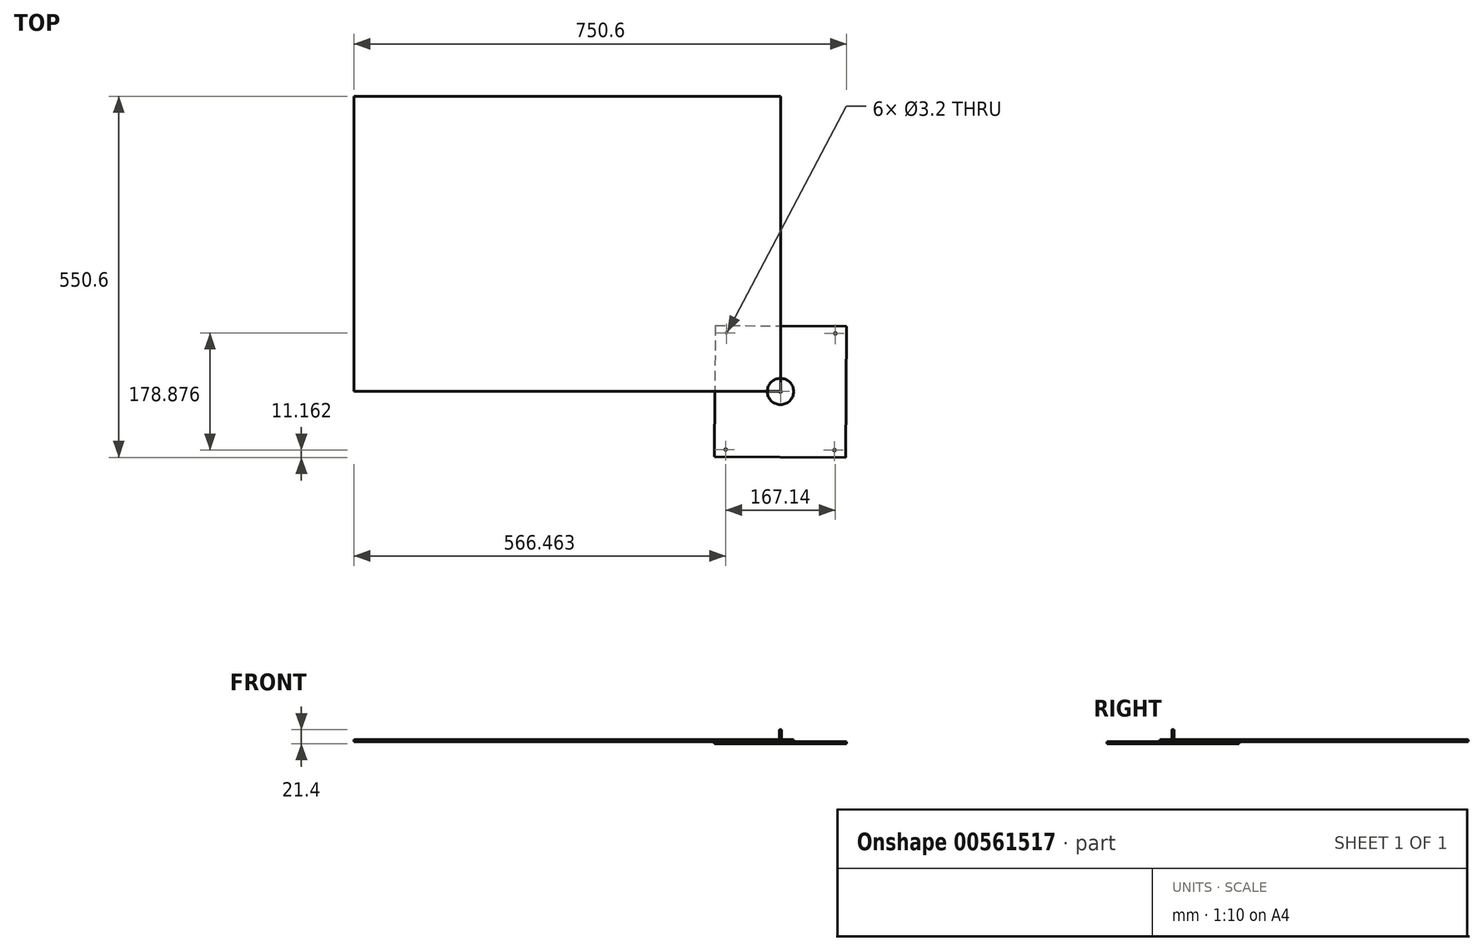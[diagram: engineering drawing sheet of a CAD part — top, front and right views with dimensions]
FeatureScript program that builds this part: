
annotation { "Feature Type Name" : "Feature", "Feature Type Description" : "" }
export const myFeature = defineFeature(function(context is Context, id is Id, definition is map)
    precondition{}
    {
        {
            var Q0;
            Q0=qCreatedBy(makeId("Top.planeOp"),FACE);
            var sketch = newSketch(context, id + "F0", { "sketchPlane" : qUnion([Q0])});
            skLineSegment(sketch, "E0.bottom", {"start": v(-99.4, 100.6) * mm, "end": v(100.6, 99.4) * mm});
            skLineSegment(sketch, "E0.top", {"start": v(-100.6, -99.4) * mm, "end": v(99.4, -100.6) * mm});
            skLineSegment(sketch, "E0.left", {"start": v(-99.4, 100.6) * mm, "end": v(-100.6, -99.4) * mm});
            skLineSegment(sketch, "E0.right", {"start": v(100.6, 99.4) * mm, "end": v(99.4, -100.6) * mm});
            skCircle(sketch, "E1", {"center": v(-83.54, -88.43) * mm, "radius": 1.6 * mm});
            skCircle(sketch, "E2", {"center": v(-82.4, 89.44) * mm, "radius": 1.6 * mm});
            skCircle(sketch, "E3", {"center": v(83.6, 88.43) * mm, "radius": 1.6 * mm});
            skCircle(sketch, "E4", {"center": v(82.4, -89.44) * mm, "radius": 1.6 * mm});
            skCircle(sketch, "E5", {"center": v(0, 0) * mm, "radius": 1.6 * mm});
            skSolve(sketch);
        }
        {
            var Q0;
            Q0=makeQuery(id+"F0.imprint","IMPRINT",FACE,{"disambiguationData":[TD([[makeQuery(id+"F0.imprint","IMPRINT",EDGE,{"derivedFrom":sQuery(id+"F0.wireOp",EDGE,"E0.bottom")}),-1.0]])]});
            extrude(context, id + "F1", {"entities" : qUnion([Q0]), "depth" : 3.2 * mm});
        }
        {
            var Q0;
            Q0=makeQuery(id+"F1.opExtrude","CAP_FACE",FACE,{"disambiguationData":[OSD([sQuery(id+"F0.wireOp",EDGE,"E0.bottom"),sQuery(id+"F0.wireOp",EDGE,"E0.top"),sQuery(id+"F0.wireOp",EDGE,"E0.left"),sQuery(id+"F0.wireOp",EDGE,"E0.right"),sQuery(id+"F0.wireOp",EDGE,"89cafc2f-88e5-4794-8ebe-84d65b012602.0"),sQuery(id+"F0.wireOp",EDGE,"89cafc2f-88e5-4794-8ebe-84d65b012602.1"),sQuery(id+"F0.wireOp",EDGE,"89cafc2f-88e5-4794-8ebe-84d65b012602.2"),sQuery(id+"F0.wireOp",EDGE,"89cafc2f-88e5-4794-8ebe-84d65b012602.3"),sQuery(id+"F0.wireOp",EDGE,"89cafc2f-88e5-4794-8ebe-84d65b012602.4"),sQuery(id+"F0.wireOp",EDGE,"89cafc2f-88e5-4794-8ebe-84d65b012602.5"),sQuery(id+"F0.wireOp",EDGE,"56885d26-f8c7-44ec-aa15-5e09e0dd8a5c.0"),sQuery(id+"F0.wireOp",EDGE,"56885d26-f8c7-44ec-aa15-5e09e0dd8a5c.1"),sQuery(id+"F0.wireOp",EDGE,"56885d26-f8c7-44ec-aa15-5e09e0dd8a5c.2"),sQuery(id+"F0.wireOp",EDGE,"56885d26-f8c7-44ec-aa15-5e09e0dd8a5c.3"),sQuery(id+"F0.wireOp",EDGE,"56885d26-f8c7-44ec-aa15-5e09e0dd8a5c.4"),sQuery(id+"F0.wireOp",EDGE,"56885d26-f8c7-44ec-aa15-5e09e0dd8a5c.5"),sQuery(id+"F0.wireOp",EDGE,"f2c23d00-8595-49d7-9619-0574d8eb3167.0"),sQuery(id+"F0.wireOp",EDGE,"f2c23d00-8595-49d7-9619-0574d8eb3167.1"),sQuery(id+"F0.wireOp",EDGE,"f2c23d00-8595-49d7-9619-0574d8eb3167.2"),sQuery(id+"F0.wireOp",EDGE,"f2c23d00-8595-49d7-9619-0574d8eb3167.3"),sQuery(id+"F0.wireOp",EDGE,"f2c23d00-8595-49d7-9619-0574d8eb3167.4"),sQuery(id+"F0.wireOp",EDGE,"f2c23d00-8595-49d7-9619-0574d8eb3167.5"),sQuery(id+"F0.wireOp",EDGE,"5ac249ba-4f04-493e-8005-cd37f262696a.0"),sQuery(id+"F0.wireOp",EDGE,"5ac249ba-4f04-493e-8005-cd37f262696a.1"),sQuery(id+"F0.wireOp",EDGE,"5ac249ba-4f04-493e-8005-cd37f262696a.2"),sQuery(id+"F0.wireOp",EDGE,"5ac249ba-4f04-493e-8005-cd37f262696a.3"),sQuery(id+"F0.wireOp",EDGE,"5ac249ba-4f04-493e-8005-cd37f262696a.4"),sQuery(id+"F0.wireOp",EDGE,"5ac249ba-4f04-493e-8005-cd37f262696a.5")])],"isStart":false});
            var sketch = newSketch(context, id + "F2", { "sketchPlane" : qUnion([Q0])});
            skCircle(sketch, "E6", {"center": v(0, 0) * mm, "radius": 20 * mm});
            skCircle(sketch, "E7", {"center": v(0, 0) * mm, "radius": 0.95 * mm});
            skSolve(sketch);
        }
        {
            var Q0;
            Q0=makeQuery(id+"F2.imprint","IMPRINT",FACE,{"disambiguationData":[TD([[makeQuery(id+"F2.imprint","IMPRINT",EDGE,{"derivedFrom":sQuery(id+"F2.wireOp",EDGE,"E6")}),1.0]])]});
            extrude(context, id + "F3", {"entities" : qUnion([Q0]), "depth" : 3.2 * mm});
        }
        {
            var Q0;
            Q0=makeQuery(id+"F3.opExtrude","CAP_FACE",FACE,{"disambiguationData":[OSD([sQuery(id+"F2.wireOp",EDGE,"E6"),sQuery(id+"F2.wireOp",EDGE,"E7")])],"isStart":false});
            var sketch = newSketch(context, id + "F4", { "sketchPlane" : qUnion([Q0])});
            skCircle(sketch, "E8", {"center": v(0, 0) * mm, "radius": 1.6 * mm});
            skSolve(sketch);
        }
        {
            var Q0;
            Q0=makeQuery(id+"F4.imprint","IMPRINT",FACE,{"disambiguationData":[TD([[makeQuery(id+"F4.imprint","IMPRINT",EDGE,{"derivedFrom":sQuery(id+"F4.wireOp",EDGE,"E8")}),1.0]])]});
            extrude(context, id + "F5", {"entities" : qUnion([Q0]), "depth" : 15 * mm, "offsetDistance" : 25 * mm});
        }
        {
            var Q0;
            Q0=makeQuery(id+"F1.opExtrude","CAP_FACE",FACE,{"disambiguationData":[OSD([sQuery(id+"F0.wireOp",EDGE,"E0.bottom"),sQuery(id+"F0.wireOp",EDGE,"E0.top"),sQuery(id+"F0.wireOp",EDGE,"E0.left"),sQuery(id+"F0.wireOp",EDGE,"E0.right"),sQuery(id+"F0.wireOp",EDGE,"E1"),sQuery(id+"F0.wireOp",EDGE,"E2"),sQuery(id+"F0.wireOp",EDGE,"E3"),sQuery(id+"F0.wireOp",EDGE,"E4"),sQuery(id+"F0.wireOp",EDGE,"E5")])],"isStart":false});
            var sketch = newSketch(context, id + "F6", { "sketchPlane" : qUnion([Q0])});
            skLineSegment(sketch, "E9.bottom", {"start": v(0, 0) * mm, "end": v(-650, 0) * mm});
            skLineSegment(sketch, "E9.top", {"start": v(0, 450) * mm, "end": v(-650, 450) * mm});
            skLineSegment(sketch, "E9.left", {"start": v(0, 0) * mm, "end": v(0, 450) * mm});
            skLineSegment(sketch, "E9.right", {"start": v(-650, 0) * mm, "end": v(-650, 450) * mm});
            skSolve(sketch);
        }
        {
            var Q0;
            Q0 = qSketchRegion(id + "F6", true);
            extrude(context, id + "F7", {"entities" : qUnion([Q0]), "depth" : 3.2 * mm, "offsetDistance" : 25 * mm});
        }
    });
